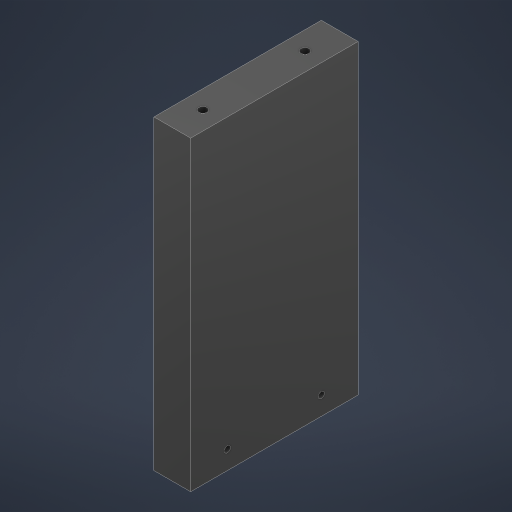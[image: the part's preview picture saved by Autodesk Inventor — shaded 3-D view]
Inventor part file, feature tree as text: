
AUTODESK INVENTOR PART (.ipt)
format: ipt  version: 2024 (Build 280153000, 153)  size: 215,040 bytes
history: native  units: in
note: dims shown in document units (in); Inventor stores cm internally (conversion verified against a paired STEP export)
features: other x1, extrude x1, sketch x1
ambient origin geometry x8: Origin, YZ Plane, XZ Plane, XY Plane, X Axis, Y Axis, Z Axis, Center Point
bodies: Body1 (feature_tree)
feature tree (3):
  other  "Sólido1"
  extrude  "Extrusión1"  Depth=0.1575in
  sketch  "Boceto1"  dims[d0=0.1575in d1=0.1575in d2=1.5748in d3=0.9843in d4=0.9843in d5=0.3543in d6=0.0in d7=5.9055in d8=0.0in]
